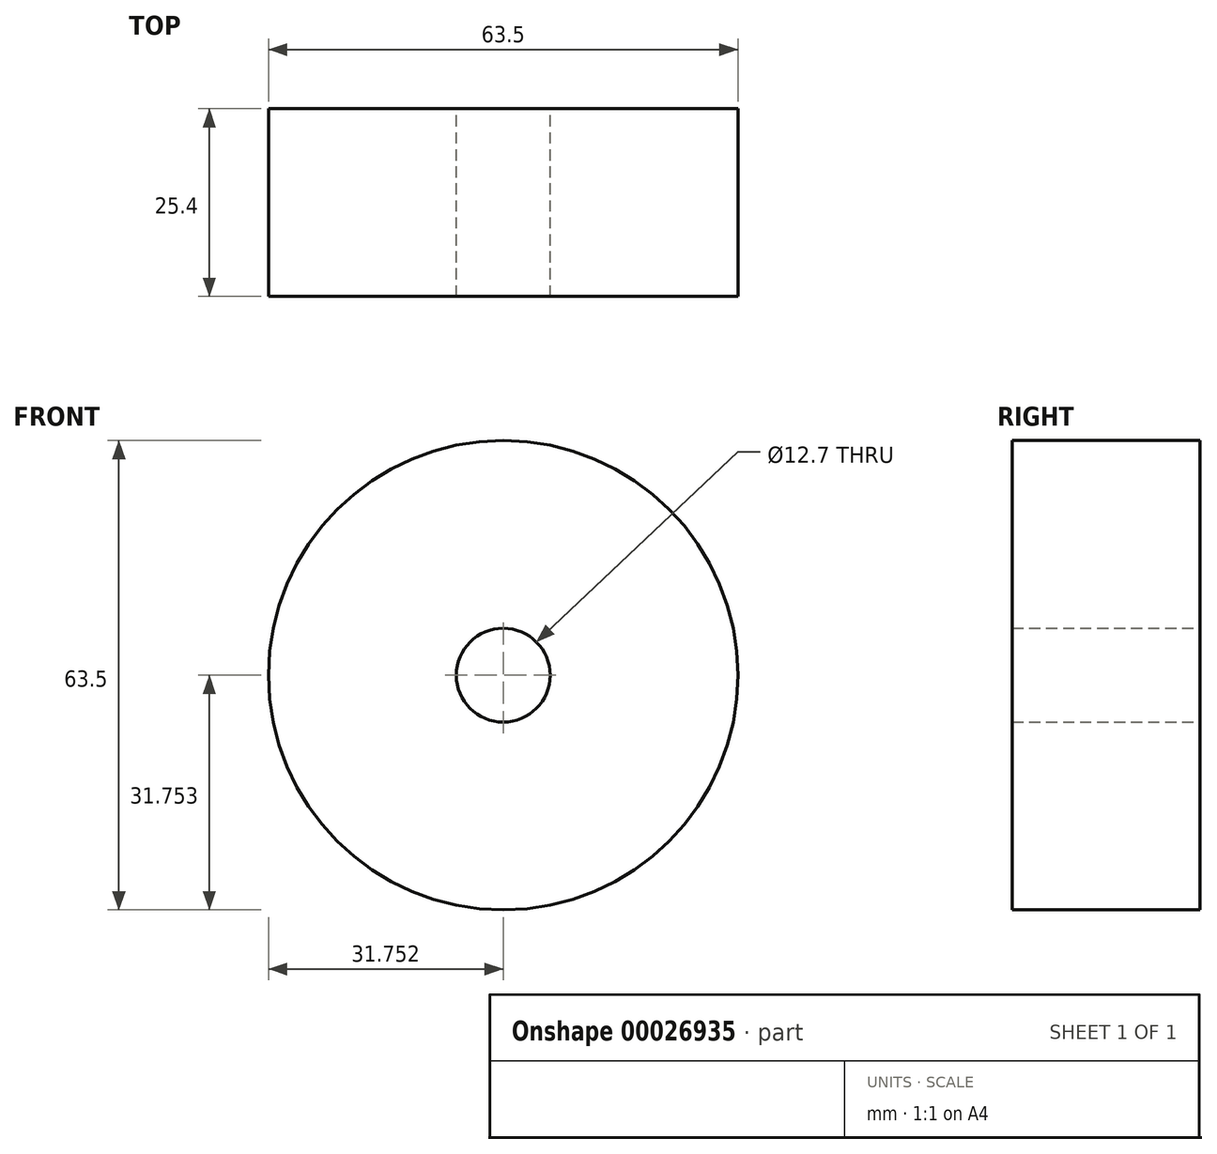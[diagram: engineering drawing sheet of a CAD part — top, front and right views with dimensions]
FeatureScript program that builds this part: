
annotation { "Feature Type Name" : "Feature", "Feature Type Description" : "" }
export const myFeature = defineFeature(function(context is Context, id is Id, definition is map)
    precondition{}
    {
        {
            var Q0;
            Q0=qCreatedBy(makeId("Front.planeOp"),FACE);
            var sketch = newSketch(context, id + "F0", { "sketchPlane" : qUnion([Q0])});
            skCircle(sketch, "E0", {"center": v(-36.98, 26.34) * mm, "radius": 31.75 * mm});
            skCircle(sketch, "E1", {"center": v(-36.98, 26.34) * mm, "radius": 6.35 * mm});
            skSolve(sketch);
        }
        {
            var Q0;
            Q0=makeQuery(id+"F0.imprint","IMPRINT",FACE,{"disambiguationData":[TD([[makeQuery(id+"F0.imprint","IMPRINT",EDGE,{"derivedFrom":sQuery(id+"F0.wireOp",EDGE,"E0")}),1.0]])]});
            extrude(context, id + "F1", {"entities" : qUnion([Q0]), "depth" : 25.4 * mm});
        }
    });
